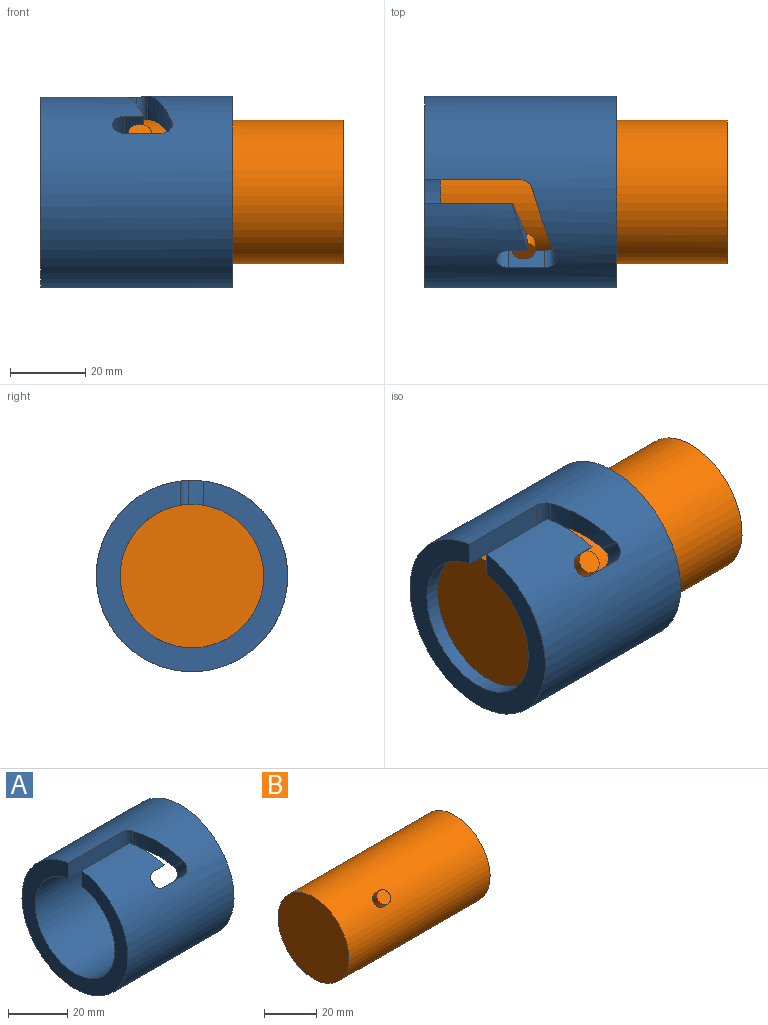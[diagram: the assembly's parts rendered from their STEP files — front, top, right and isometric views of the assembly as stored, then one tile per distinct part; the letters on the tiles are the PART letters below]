
ASSEMBLY  parts=2 mates=1
PART A: 13 faces, bbox 50.8x50.8x51.1 mm
  f0: cylinder r=19.05mm len=50.8mm, axis (-1,0,0), area 5745mm2, adj f2,f3,f4,f5,f6,f7,f8,f9
  f1: cylinder r=25.4mm len=50.8mm, axis (-1,0,0), area 7741.5mm2, adj f2,f3,f4,f5,f6,f7,f8,f9
  f2: plane 50.8x50.8mm, normal (1,0,0), area 886.7mm2, adj f0,f1
  f3: plane 50.8x50.6mm, normal (-1,0,0), area 846.3mm2, adj f0,f1,f5,f6
  f4: cylinder r=3.17mm len=6.6mm, axis (0,0,-1), area 25.6mm2, adj f0,f1,f5,f12
  f5: plane 25.4x6.42mm, normal (0,-1,0), area 163mm2, adj f0,f1,f3,f4
  f6: plane 23.31x6.42mm, normal (0,1,0), area 148.7mm2, adj f0,f1,f3,f11
  f7: cylinder r=3.17mm len=8.01mm, axis (0,0.71,-0.71), area 39.9mm2, adj f0,f1,f8,f12
  f8: plane 9.53x4.54mm, normal (0,0.71,0.71), area 61.1mm2, adj f0,f1,f7,f9
  f9: cylinder r=3.17mm len=9.17mm, axis (0,0.71,-0.71), area 63.7mm2, adj f0,f1,f8,f10
  f10: plane 5.17x4.54mm, normal (0,-0.71,-0.71), area 31.9mm2, adj f0,f1,f9,f11
  f11: bspline ~21.52x18.75mm, area 74.9mm2, adj f0,f1,f6,f10
  f12: bspline ~22.48x17.34mm, area 116.1mm2, adj f0,f1,f4,f7
PART B: 5 faces, bbox 76.2x38.1x38.1 mm
  f0: cylinder r=19.05mm len=76.2mm, axis (-1,0,0), area 9091.4mm2, adj f1,f2,f4
  f1: plane 38.1x38.1mm, normal (1,0,0), area 1140.1mm2, adj f0
  f2: plane 38.1x38.1mm, normal (-1,0,0), area 1140.1mm2, adj f0
  f3: plane 6.1x4.31mm, normal (0,-0.71,0.71), area 29.2mm2, adj f4
  f4: cylinder r=3.05mm len=6.73mm, axis (0,-0.71,0.71), area 63.2mm2, adj f0,f3
PLACE A at identity fixed
PLACE B rot(axis=(-1,0,0),0.3deg) t=(4.02,0,0)mm
MATE cylindrical B.f0 <-> A.f0  axis (-1,0,0) through (42.12,0,0)mm
